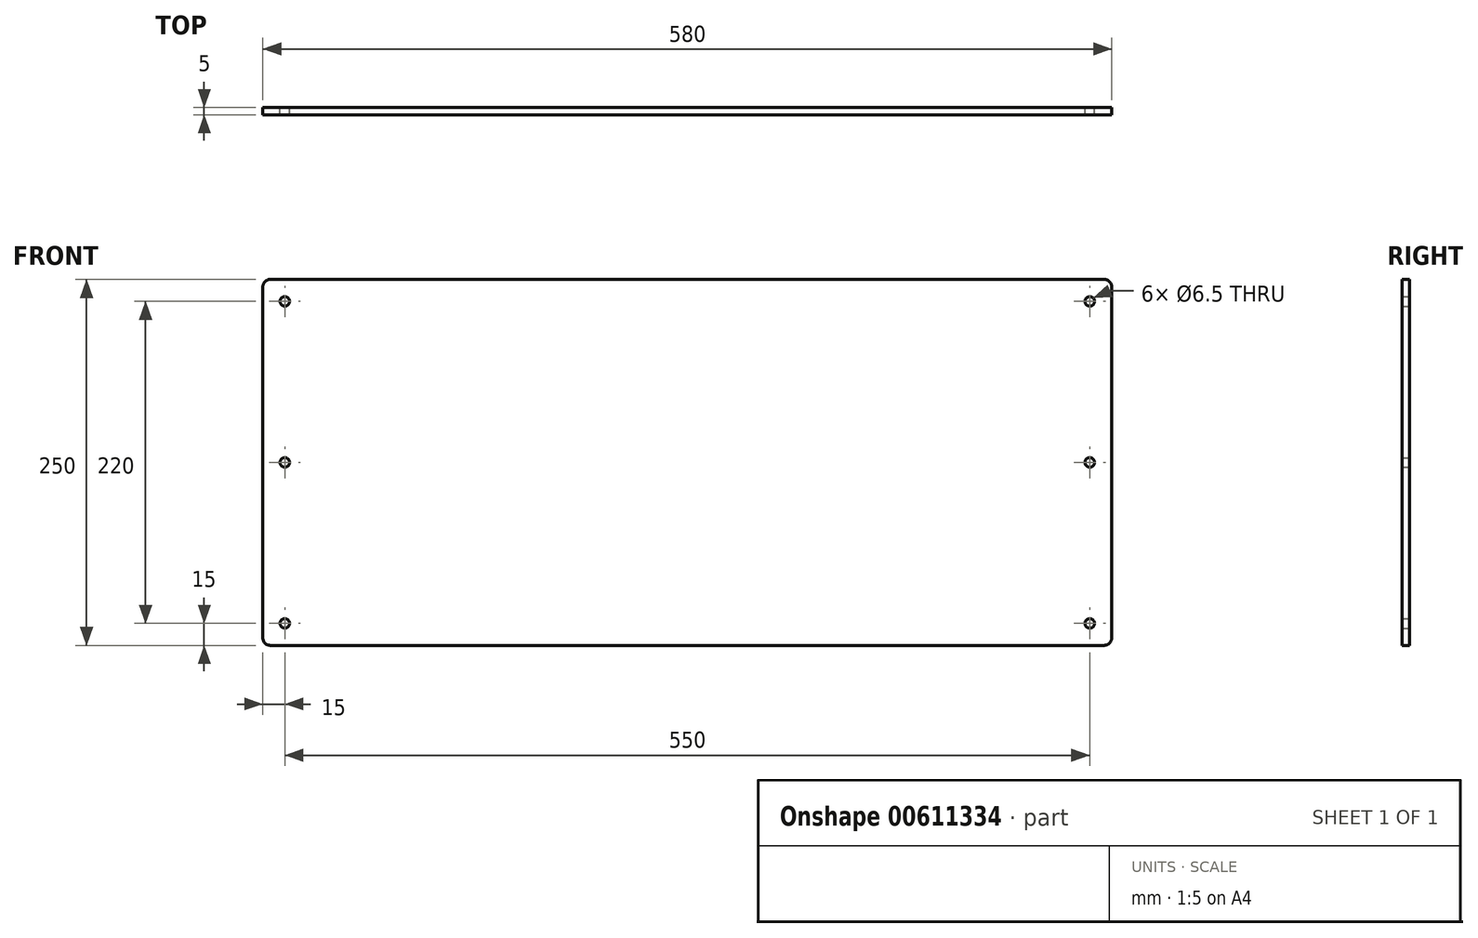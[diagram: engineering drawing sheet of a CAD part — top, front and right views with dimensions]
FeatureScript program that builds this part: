
annotation { "Feature Type Name" : "Feature", "Feature Type Description" : "" }
export const myFeature = defineFeature(function(context is Context, id is Id, definition is map)
    precondition{}
    {
        {
            var Q0;
            Q0=qCreatedBy(makeId("Front.planeOp"),FACE);
            var sketch = newSketch(context, id + "F0", { "sketchPlane" : qUnion([Q0])});
            skLineSegment(sketch, "E0.bottom", {"start": v(0, 0) * mm, "end": v(580, 0) * mm});
            skLineSegment(sketch, "E0.top", {"start": v(0, 250) * mm, "end": v(580, 250) * mm});
            skLineSegment(sketch, "E0.left", {"start": v(0, 0) * mm, "end": v(0, 250) * mm});
            skLineSegment(sketch, "E0.right", {"start": v(580, 0) * mm, "end": v(580, 250) * mm});
            skCircle(sketch, "E1", {"center": v(15, 15) * mm, "radius": 3.25 * mm});
            skCircle(sketch, "E2", {"center": v(15, 125) * mm, "radius": 3.25 * mm});
            skCircle(sketch, "E3", {"center": v(15, 235) * mm, "radius": 3.25 * mm});
            skCircle(sketch, "E4", {"center": v(565, 15) * mm, "radius": 3.25 * mm});
            skCircle(sketch, "E5", {"center": v(565, 125) * mm, "radius": 3.25 * mm});
            skCircle(sketch, "E6", {"center": v(565, 235) * mm, "radius": 3.25 * mm});
            skSolve(sketch);
        }
        {
            var Q0;
            Q0=makeQuery(id+"F0.imprint","IMPRINT",FACE,{"disambiguationData":[TD([[makeQuery(id+"F0.imprint","IMPRINT",EDGE,{"derivedFrom":sQuery(id+"F0.wireOp",EDGE,"E0.bottom")}),1.0]])]});
            extrude(context, id + "F1", {"entities" : qUnion([Q0]), "depth" : 5 * mm, "offsetDistance" : 25 * mm});
        }
        {
            var Q0;
            Q0=makeQuery(id+"F1.opExtrude","SWEPT_EDGE",EDGE,{"disambiguationData":[OSD([sQuery(id+"F0.wireOp",EDGE,"E0.top"),sQuery(id+"F0.wireOp",EDGE,"E0.left")])]});
            var Q1;
            Q1=makeQuery(id+"F1.opExtrude","SWEPT_EDGE",EDGE,{"disambiguationData":[OSD([sQuery(id+"F0.wireOp",EDGE,"E0.bottom"),sQuery(id+"F0.wireOp",EDGE,"E0.left")])]});
            var Q2;
            Q2=makeQuery(id+"F1.opExtrude","SWEPT_EDGE",EDGE,{"disambiguationData":[OSD([sQuery(id+"F0.wireOp",EDGE,"E0.bottom"),sQuery(id+"F0.wireOp",EDGE,"E0.right")])]});
            var Q3;
            Q3=makeQuery(id+"F1.opExtrude","SWEPT_EDGE",EDGE,{"disambiguationData":[OSD([sQuery(id+"F0.wireOp",EDGE,"E0.top"),sQuery(id+"F0.wireOp",EDGE,"E0.right")])]});
            fillet(context, id + "F2", {"entities" : qUnion([Q0, Q1, Q2, Q3]), "radius" : 5 * mm, "tangentPropagation" : true, "allowEdgeOverflow" : false});
        }
    });
